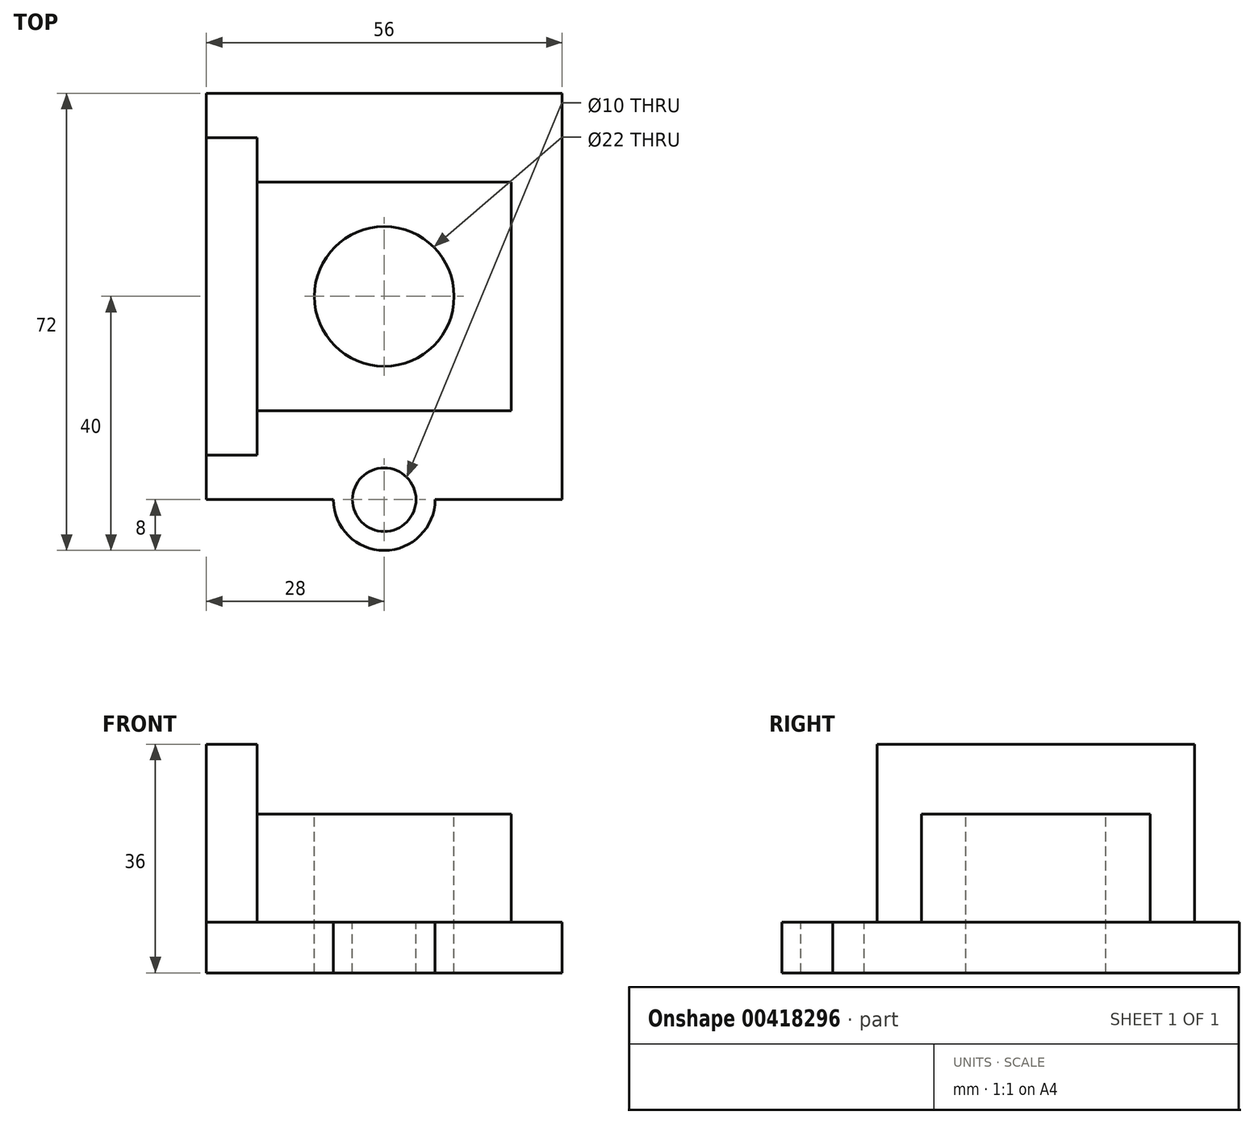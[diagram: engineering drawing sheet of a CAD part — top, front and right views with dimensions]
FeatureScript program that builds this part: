
annotation { "Feature Type Name" : "Feature", "Feature Type Description" : "" }
export const myFeature = defineFeature(function(context is Context, id is Id, definition is map)
    precondition{}
    {
        {
            var Q0;
            Q0=qCreatedBy(makeId("Top.planeOp"),FACE);
            var sketch = newSketch(context, id + "F0", { "sketchPlane" : qUnion([Q0])});
            skLineSegment(sketch, "E0.bottom", {"start": v(-28, 32) * mm, "end": v(28, 32) * mm});
            skLineSegment(sketch, "E0.top", {"start": v(-28, -32) * mm, "end": v(28, -32) * mm});
            skLineSegment(sketch, "E0.left", {"start": v(-28, 32) * mm, "end": v(-28, -32) * mm});
            skLineSegment(sketch, "E0.right", {"start": v(28, 32) * mm, "end": v(28, -32) * mm});
            skPoint(sketch, "E0.middle", {"position": v(0, 0) * mm});
            skSolve(sketch);
        }
        {
            var Q0;
            Q0 = qSketchRegion(id + "F0", true);
            extrude(context, id + "F1", {"entities" : qUnion([Q0]), "oppositeDirection" : true, "depth" : 8 * mm});
        }
        {
            var Q0;
            Q0=makeQuery(id+"F1.opExtrude","CAP_FACE",FACE,{"disambiguationData":[OSD([sQuery(id+"F0.wireOp",EDGE,"E0.bottom"),sQuery(id+"F0.wireOp",EDGE,"E0.top"),sQuery(id+"F0.wireOp",EDGE,"E0.left"),sQuery(id+"F0.wireOp",EDGE,"E0.right")])],"isStart":true});
            var sketch = newSketch(context, id + "F2", { "sketchPlane" : qUnion([Q0])});
            skLineSegment(sketch, "E1.bottom", {"start": v(-28, 25) * mm, "end": v(-20, 25) * mm});
            skLineSegment(sketch, "E1.top", {"start": v(-28, -25) * mm, "end": v(-20, -25) * mm});
            skLineSegment(sketch, "E1.left", {"start": v(-28, 25) * mm, "end": v(-28, -25) * mm});
            skLineSegment(sketch, "E1.right", {"start": v(-20, 25) * mm, "end": v(-20, -25) * mm});
            skSolve(sketch);
        }
        {
            var Q0;
            Q0 = qSketchRegion(id + "F2", true);
            extrude(context, id + "F3", {"entities" : qUnion([Q0]), "operationType" : NewBodyOperationType.ADD, "depth" : (36 - 8) * mm});
        }
        {
            var Q0;
            Q0=makeQuery(id+"F1.opExtrude","CAP_FACE",FACE,{"disambiguationData":[OSD([sQuery(id+"F0.wireOp",EDGE,"E0.bottom"),sQuery(id+"F0.wireOp",EDGE,"E0.top"),sQuery(id+"F0.wireOp",EDGE,"E0.left"),sQuery(id+"F0.wireOp",EDGE,"E0.right")])],"isStart":true});
            var sketch = newSketch(context, id + "F4", { "sketchPlane" : qUnion([Q0])});
            skCircle(sketch, "E2", {"center": v(0, -32) * mm, "radius": 8 * mm});
            skSolve(sketch);
        }
        {
            var Q0;
            Q0 = qSketchRegion(id + "F4", true);
            var Q1;
            Q1=makeQuery(id+"F1.opExtrude","CAP_FACE",FACE,{"disambiguationData":[OSD([sQuery(id+"F0.wireOp",EDGE,"E0.bottom"),sQuery(id+"F0.wireOp",EDGE,"E0.top"),sQuery(id+"F0.wireOp",EDGE,"E0.left"),sQuery(id+"F0.wireOp",EDGE,"E0.right")])],"isStart":false});
            extrude(context, id + "F5", {"entities" : qUnion([Q0]), "operationType" : NewBodyOperationType.ADD, "endBound" : BoundingType.UP_TO_SURFACE, "oppositeDirection" : true, "endBoundEntityFace" : qUnion([Q1]), "depth" : 25 * mm});
        }
        {
            var Q0;
            Q0=makeQuery(id+"F5.boolean.opBoolean","MERGE",FACE,{"derivedFrom":[makeQuery(id+"F1.opExtrude","CAP_FACE",FACE,{"disambiguationData":[OSD([sQuery(id+"F0.wireOp",EDGE,"E0.bottom"),sQuery(id+"F0.wireOp",EDGE,"E0.top"),sQuery(id+"F0.wireOp",EDGE,"E0.left"),sQuery(id+"F0.wireOp",EDGE,"E0.right")])],"isStart":true}),makeQuery(id+"F5.opExtrude","CAP_FACE",FACE,{"disambiguationData":[OSD([sQuery(id+"F4.wireOp",EDGE,"E2")])],"isStart":true})]});
            var sketch = newSketch(context, id + "F6", { "sketchPlane" : qUnion([Q0])});
            skCircle(sketch, "E3", {"center": v(0, -32) * mm, "radius": 5 * mm});
            skSolve(sketch);
        }
        {
            var Q0;
            Q0 = qSketchRegion(id + "F6", true);
            extrude(context, id + "F7", {"entities" : qUnion([Q0]), "operationType" : NewBodyOperationType.REMOVE, "endBound" : BoundingType.THROUGH_ALL, "oppositeDirection" : true, "depth" : 25 * mm});
        }
        {
            var Q0;
            {var subQ0=sQuery(id+"F4.wireOp",EDGE,"E2");Q0=makeQuery(id+"FYWMMFnygUz84bn_1.1.F5.boolean.opBoolean","MERGE",FACE,{"derivedFrom":[makeQuery(id+"F5.boolean.opBoolean","MERGE",FACE,{"derivedFrom":[makeQuery(id+"F1.opExtrude","CAP_FACE",FACE,{"disambiguationData":[OSD([sQuery(id+"F0.wireOp",EDGE,"E0.bottom"),sQuery(id+"F0.wireOp",EDGE,"E0.top"),sQuery(id+"F0.wireOp",EDGE,"E0.left"),sQuery(id+"F0.wireOp",EDGE,"E0.right")])],"isStart":true}),makeQuery(id+"F5.opExtrude","CAP_FACE",FACE,{"disambiguationData":[OSD([subQ0])],"isStart":true})]}),makeQuery(id+"FYWMMFnygUz84bn_1.1.F5.opExtrude","CAP_FACE",FACE,{"disambiguationData":[OSD([subQ0])],"isStart":true})]});}
            var sketch = newSketch(context, id + "F8", { "sketchPlane" : qUnion([Q0])});
            skLineSegment(sketch, "E4.bottom", {"start": v(-20, 18) * mm, "end": v(20, 18) * mm});
            skLineSegment(sketch, "E4.top", {"start": v(-20, -18) * mm, "end": v(20, -18) * mm});
            skLineSegment(sketch, "E4.left", {"start": v(-20, 18) * mm, "end": v(-20, -18) * mm});
            skLineSegment(sketch, "E4.right", {"start": v(20, 18) * mm, "end": v(20, -18) * mm});
            skPoint(sketch, "E4.middle", {"position": v(0, 0) * mm});
            skSolve(sketch);
        }
        {
            var Q0;
            Q0 = qSketchRegion(id + "F8", true);
            extrude(context, id + "F9", {"entities" : qUnion([Q0]), "operationType" : NewBodyOperationType.ADD, "depth" : 17 * mm});
        }
        {
            var Q0;
            Q0=makeQuery(id+"F9.opExtrude","CAP_FACE",FACE,{"disambiguationData":[OSD([sQuery(id+"F8.wireOp",EDGE,"E4.bottom"),sQuery(id+"F8.wireOp",EDGE,"E4.top"),sQuery(id+"F8.wireOp",EDGE,"E4.left"),sQuery(id+"F8.wireOp",EDGE,"E4.right")])],"isStart":false});
            var sketch = newSketch(context, id + "F10", { "sketchPlane" : qUnion([Q0])});
            skCircle(sketch, "E5", {"center": v(0, 0) * mm, "radius": 11 * mm});
            skSolve(sketch);
        }
        {
            var Q0;
            Q0 = qSketchRegion(id + "F10", true);
            extrude(context, id + "F11", {"entities" : qUnion([Q0]), "operationType" : NewBodyOperationType.REMOVE, "endBound" : BoundingType.THROUGH_ALL, "oppositeDirection" : true, "depth" : 25 * mm});
        }
    });
